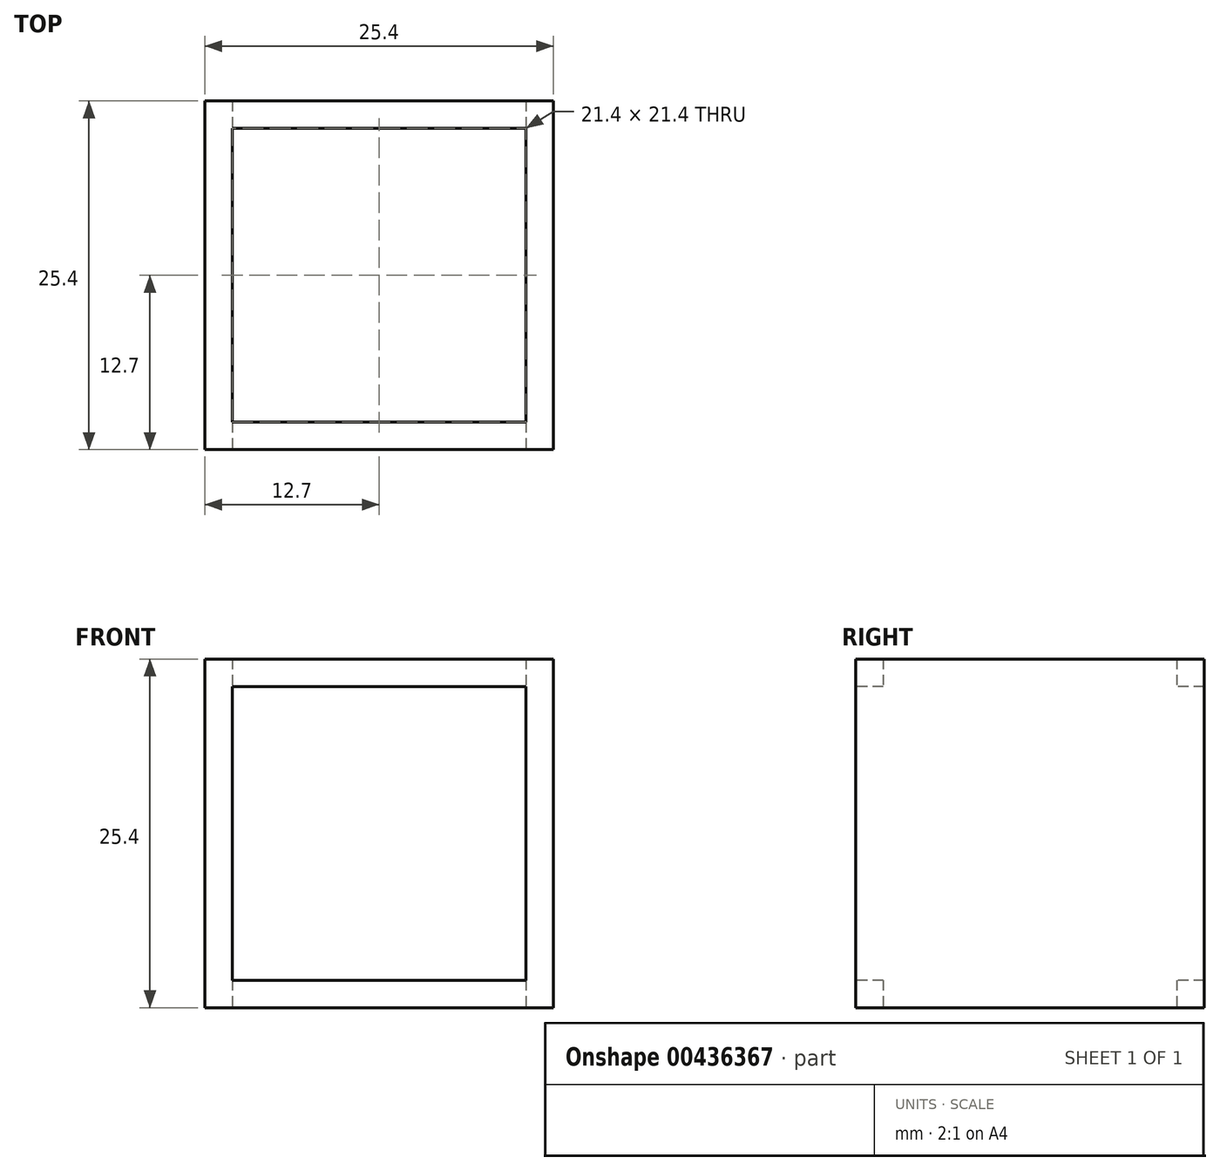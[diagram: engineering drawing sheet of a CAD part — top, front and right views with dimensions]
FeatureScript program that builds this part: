
annotation { "Feature Type Name" : "Feature", "Feature Type Description" : "" }
export const myFeature = defineFeature(function(context is Context, id is Id, definition is map)
    precondition{}
    {
        {
            var Q0;
            Q0=qCreatedBy(makeId("Top.planeOp"),FACE);
            var sketch = newSketch(context, id + "F0", { "sketchPlane" : qUnion([Q0])});
            skLineSegment(sketch, "E0.bottom", {"start": v(-12.7, 12.7) * mm, "end": v(12.7, 12.7) * mm});
            skLineSegment(sketch, "E0.top", {"start": v(-12.7, -12.7) * mm, "end": v(12.7, -12.7) * mm});
            skLineSegment(sketch, "E0.left", {"start": v(-12.7, 12.7) * mm, "end": v(-12.7, -12.7) * mm});
            skLineSegment(sketch, "E0.right", {"start": v(12.7, 12.7) * mm, "end": v(12.7, -12.7) * mm});
            skLineSegment(sketch, "E1", {"start": v(0, 0) * mm, "end": v(0, 12.7) * mm, "construction": true});
            skLineSegment(sketch, "E2", {"start": v(0, 0) * mm, "end": v(12.7, 0) * mm, "construction": true});
            skLineSegment(sketch, "E3.0", {"start": v(-10.7, 10.7) * mm, "end": v(10.7, 10.7) * mm});
            skLineSegment(sketch, "E3.1", {"start": v(-10.7, 10.7) * mm, "end": v(-10.7, -10.7) * mm});
            skLineSegment(sketch, "E3.2", {"start": v(-10.7, -10.7) * mm, "end": v(10.7, -10.7) * mm});
            skLineSegment(sketch, "E3.3", {"start": v(10.7, 10.7) * mm, "end": v(10.7, -10.7) * mm});
            skSolve(sketch);
        }
        {
            var Q0;
            Q0=makeQuery(id+"F0.imprint","IMPRINT",FACE,{"disambiguationData":[TD([[makeQuery(id+"F0.imprint","IMPRINT",EDGE,{"derivedFrom":sQuery(id+"F0.wireOp",EDGE,"E0.bottom")}),-1.0]])]});
            extrude(context, id + "F1", {"entities" : qUnion([Q0]), "depth" : 25.4 * mm});
        }
        {
            var Q0;
            Q0=makeQuery(id+"F1.opExtrude","SWEPT_FACE",FACE,{"disambiguationData":[OSD([sQuery(id+"F0.wireOp",EDGE,"E0.top")])]});
            var sketch = newSketch(context, id + "F2", { "sketchPlane" : qUnion([Q0])});
            skLineSegment(sketch, "E4.0", {"start": v(-10.7, 23.4) * mm, "end": v(10.7, 23.4) * mm});
            skLineSegment(sketch, "E4.1", {"start": v(-10.7, 23.4) * mm, "end": v(-10.7, 2) * mm});
            skLineSegment(sketch, "E4.2", {"start": v(-10.7, 2) * mm, "end": v(10.7, 2) * mm});
            skLineSegment(sketch, "E4.3", {"start": v(10.7, 23.4) * mm, "end": v(10.7, 2) * mm});
            skSolve(sketch);
        }
        {
            var Q0;
            Q0 = qSketchRegion(id + "F2", true);
            extrude(context, id + "F3", {"entities" : qUnion([Q0]), "operationType" : NewBodyOperationType.REMOVE, "endBound" : BoundingType.THROUGH_ALL, "oppositeDirection" : true, "depth" : 25.4 * mm});
        }
        {
            var Q0;
            Q0=qCreatedBy(makeId("Front.planeOp"),FACE);
            var sketch = newSketch(context, id + "F4", { "sketchPlane" : qUnion([Q0])});
            skLineSegment(sketch, "E5", {"start": v(0, 40.41) * mm, "end": v(0, -11.51) * mm, "construction": true});
            skSolve(sketch);
        }
    });
